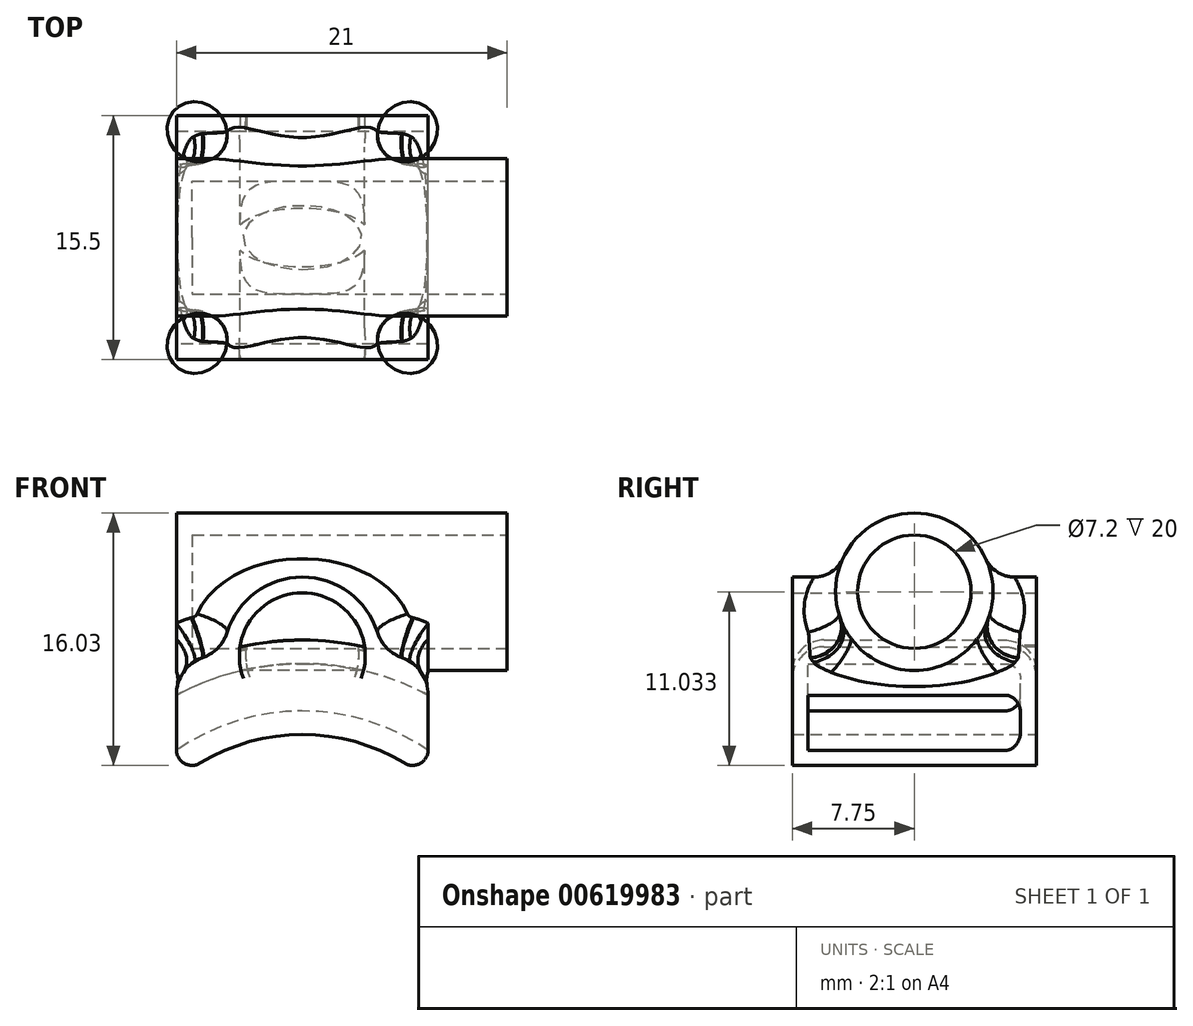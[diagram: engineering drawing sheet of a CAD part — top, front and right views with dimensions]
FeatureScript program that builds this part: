
annotation { "Feature Type Name" : "Feature", "Feature Type Description" : "" }
export const myFeature = defineFeature(function(context is Context, id is Id, definition is map)
    precondition{}
    {
        {
            var Q0;
            Q0=qCreatedBy(makeId("Front.planeOp"),FACE);
            var sketch = newSketch(context, id + "F0", { "sketchPlane" : qUnion([Q0])});
            skArc(sketch, "E0", {"start": v(8, 9.6) * mm, "mid": v(0, 12.5) * mm, "end": v(-8, 9.6) * mm});
            skArc(sketch, "E1.0", {"start": v(8, 11.49) * mm, "mid": v(0, 14) * mm, "end": v(-8, 11.49) * mm});
            skLineSegment(sketch, "E2", {"start": v(-8, 11.49) * mm, "end": v(-8, 9.6) * mm});
            skLineSegment(sketch, "E3", {"start": v(8, 11.49) * mm, "end": v(8, 9.6) * mm});
            skArc(sketch, "E4.0", {"start": v(8, 15) * mm, "mid": v(0, 17) * mm, "end": v(-8, 15) * mm});
            skLineSegment(sketch, "E5", {"start": v(-8, 15) * mm, "end": v(-8, 16.68) * mm});
            skLineSegment(sketch, "E6", {"start": v(8, 15) * mm, "end": v(8, 16.68) * mm});
            skArc(sketch, "E7.0", {"start": v(8, 16.68) * mm, "mid": v(0, 18.5) * mm, "end": v(-8, 16.68) * mm});
            skPoint(sketch, "E8.end.orphan", {"position": v(-8, 29.56) * mm});
            skPoint(sketch, "E8.start.orphan", {"position": v(8, 29.56) * mm});
            skArc(sketch, "E9", {"start": v(5, 17.81) * mm, "mid": v(0, 22.5) * mm, "end": v(-5, 17.81) * mm});
            skPoint(sketch, "E9.centerSnap0", {"position": v(0, 17) * mm});
            skArc(sketch, "E10.0", {"start": v(3.96, 18.07) * mm, "mid": v(0, 21.5) * mm, "end": v(-3.96, 18.07) * mm});
            skSolve(sketch);
        }
        {
            var Q0;
            Q0=qSketchRegion(id+"F0",true);
            extrude(context, id + "F1", {"entities" : qUnion([Q0]), "depth" : 13.5 * mm, "offsetDistance" : 25 * mm});
        }
        {
            var Q0;
            Q0=makeQuery(id+"F1.opExtrude","CAP_FACE",FACE,{"disambiguationData":[OSD([sQuery(id+"F0.wireOp",EDGE,"E0"),sQuery(id+"F0.wireOp",EDGE,"E1.0"),sQuery(id+"F0.wireOp",EDGE,"E2"),sQuery(id+"F0.wireOp",EDGE,"E3")])],"isStart":true});
            var sketch = newSketch(context, id + "F2", { "sketchPlane" : qUnion([Q0])});
            skCircle(sketch, "E11", {"center": v(0, 17.5) * mm, "radius": 3.6 * mm});
            skPoint(sketch, "E11.centerSnap0", {"position": v(0, 14) * mm});
            skCircle(sketch, "E12", {"center": v(0, 17.5) * mm, "radius": 5 * mm});
            skSolve(sketch);
        }
        {
            var Q0;
            Q0=qSketchRegion(id+"F2",true);
            extrude(context, id + "F3", {"entities" : qUnion([Q0]), "depth" : 1 * mm, "offsetDistance" : 25 * mm});
        }
        {
            var Q0;
            Q0=makeQuery(id+"F1.opExtrude","CAP_FACE",FACE,{"disambiguationData":[OSD([sQuery(id+"F0.wireOp",EDGE,"E4.0"),sQuery(id+"F0.wireOp",EDGE,"E5"),sQuery(id+"F0.wireOp",EDGE,"E6"),sQuery(id+"F0.wireOp",EDGE,"E7.0"),sQuery(id+"F0.wireOp",EDGE,"E9"),sQuery(id+"F0.wireOp",EDGE,"E10.0")])],"isStart":true});
            var sketch = newSketch(context, id + "F4", { "sketchPlane" : qUnion([Q0])});
            skArc(sketch, "E13.0", {"start": v(-3.54, 18.16) * mm, "mid": v(0, 13.9) * mm, "end": v(3.54, 18.16) * mm});
            skArc(sketch, "E14.0", {"start": v(-3.54, 18.16) * mm, "mid": v(0, 18.5) * mm, "end": v(3.54, 18.16) * mm});
            skSolve(sketch);
        }
        {
            var Q0;
            Q0=qSketchRegion(id+"F4",true);
            extrude(context, id + "F5", {"entities" : qUnion([Q0]), "depth" : 1 * mm, "offsetDistance" : 25 * mm});
        }
        {
            var Q0;
            Q0=makeQuery(id+"F1.opExtrude","CAP_FACE",FACE,{"disambiguationData":[OSD([sQuery(id+"F0.wireOp",EDGE,"E0"),sQuery(id+"F0.wireOp",EDGE,"E1.0"),sQuery(id+"F0.wireOp",EDGE,"E2"),sQuery(id+"F0.wireOp",EDGE,"E3")])],"isStart":true});
            var sketch = newSketch(context, id + "F6", { "sketchPlane" : qUnion([Q0])});
            skLineSegment(sketch, "E15.0", {"start": v(-8, 11.49) * mm, "end": v(-8, 9.6) * mm});
            skLineSegment(sketch, "E15.2", {"start": v(8, 9.6) * mm, "end": v(8, 11.49) * mm});
            skArc(sketch, "E15.3", {"start": v(-8, 9.6) * mm, "mid": v(0, 12.5) * mm, "end": v(8, 9.6) * mm});
            skArc(sketch, "E16.0", {"start": v(-8, 16.68) * mm, "mid": v(-6.52, 17.31) * mm, "end": v(-5, 17.81) * mm});
            skArc(sketch, "E17.0", {"start": v(5, 17.81) * mm, "mid": v(6.52, 17.31) * mm, "end": v(8, 16.68) * mm});
            skLineSegment(sketch, "E18.0", {"start": v(-8, 15) * mm, "end": v(-8, 16.68) * mm});
            skLineSegment(sketch, "E19.0", {"start": v(8, 15) * mm, "end": v(8, 16.68) * mm});
            skArc(sketch, "E20.0", {"start": v(-5, 17.81) * mm, "mid": v(0, 12.5) * mm, "end": v(5, 17.81) * mm});
            skLineSegment(sketch, "E21", {"start": v(-8, 15) * mm, "end": v(-8, 11.49) * mm});
            skLineSegment(sketch, "E22", {"start": v(8, 15) * mm, "end": v(8, 11.49) * mm});
            skSolve(sketch);
        }
        {
            var Q0;
            Q0=qSketchRegion(id+"F6",true);
            extrude(context, id + "F7", {"entities" : qUnion([Q0]), "depth" : 1 * mm, "offsetDistance" : 25 * mm});
        }
        {
            var Q0;
            Q0=makeQuery(id+"F1.opExtrude","CAP_FACE",FACE,{"disambiguationData":[OSD([sQuery(id+"F0.wireOp",EDGE,"E0"),sQuery(id+"F0.wireOp",EDGE,"E1.0"),sQuery(id+"F0.wireOp",EDGE,"E2"),sQuery(id+"F0.wireOp",EDGE,"E3")])],"isStart":false});
            var sketch = newSketch(context, id + "F8", { "sketchPlane" : qUnion([Q0])});
            skArc(sketch, "E23.0", {"start": v(8, 9.6) * mm, "mid": v(0, 12.5) * mm, "end": v(-8, 9.6) * mm});
            skArc(sketch, "E24.0", {"start": v(8, 16.68) * mm, "mid": v(0, 18.5) * mm, "end": v(-8, 16.68) * mm});
            skLineSegment(sketch, "E25", {"start": v(-8, 9.6) * mm, "end": v(-8, 16.68) * mm});
            skLineSegment(sketch, "E26", {"start": v(8, 9.6) * mm, "end": v(8, 16.68) * mm});
            skArc(sketch, "E27.0", {"start": v(5, 17.81) * mm, "mid": v(0, 22.5) * mm, "end": v(-5, 17.81) * mm});
            skArc(sketch, "E28.0", {"start": v(3.96, 18.07) * mm, "mid": v(0, 21.5) * mm, "end": v(-3.96, 18.07) * mm});
            skSolve(sketch);
        }
        {
            var Q0;
            Q0=qSketchRegion(id+"F8",true);
            extrude(context, id + "F9", {"entities" : qUnion([Q0]), "depth" : 1 * mm, "offsetDistance" : 25 * mm});
        }
        {
            var Q0;
            Q0=makeQuery(id+"F1.opExtrude","SWEPT_BODY",BODY,{"disambiguationData":[OSD([sQuery(id+"F0.wireOp",EDGE,"E4.0"),sQuery(id+"F0.wireOp",EDGE,"E5"),sQuery(id+"F0.wireOp",EDGE,"E6"),sQuery(id+"F0.wireOp",EDGE,"E7.0"),sQuery(id+"F0.wireOp",EDGE,"E9"),sQuery(id+"F0.wireOp",EDGE,"E10.0")])]});
            var Q1;
            Q1=makeQuery(id+"F3.opExtrude","SWEPT_BODY",BODY,{"disambiguationData":[OSD([sQuery(id+"F2.wireOp",EDGE,"E11"),sQuery(id+"F2.wireOp",EDGE,"E12")])]});
            var Q2;
            Q2=makeQuery(id+"F1.opExtrude","SWEPT_BODY",BODY,{"disambiguationData":[OSD([sQuery(id+"F0.wireOp",EDGE,"E0"),sQuery(id+"F0.wireOp",EDGE,"E1.0"),sQuery(id+"F0.wireOp",EDGE,"E2"),sQuery(id+"F0.wireOp",EDGE,"E3")])]});
            var Q3;
            Q3=makeQuery(id+"F7.opExtrude","SWEPT_BODY",BODY,{"disambiguationData":[OSD([sQuery(id+"F6.wireOp",EDGE,"E15.2"),sQuery(id+"F6.wireOp",EDGE,"E15.3"),sQuery(id+"F6.wireOp",EDGE,"E17.0"),sQuery(id+"F6.wireOp",EDGE,"E19.0"),sQuery(id+"F6.wireOp",EDGE,"E20.0"),sQuery(id+"F6.wireOp",EDGE,"E22")])]});
            var Q4;
            Q4=makeQuery(id+"F7.opExtrude","SWEPT_BODY",BODY,{"disambiguationData":[OSD([sQuery(id+"F6.wireOp",EDGE,"E15.0"),sQuery(id+"F6.wireOp",EDGE,"E15.3"),sQuery(id+"F6.wireOp",EDGE,"E16.0"),sQuery(id+"F6.wireOp",EDGE,"E18.0"),sQuery(id+"F6.wireOp",EDGE,"E20.0"),sQuery(id+"F6.wireOp",EDGE,"E21")])]});
            var Q5;
            Q5=makeQuery(id+"F5.opExtrude","SWEPT_BODY",BODY,{"disambiguationData":[OSD([sQuery(id+"F4.wireOp",EDGE,"E13.0"),sQuery(id+"F4.wireOp",EDGE,"E14.0")])]});
            var Q6;
            Q6=makeQuery(id+"F9.opExtrude","SWEPT_BODY",BODY,{"disambiguationData":[OSD([sQuery(id+"F8.wireOp",EDGE,"E23.0"),sQuery(id+"F8.wireOp",EDGE,"E24.0"),sQuery(id+"F8.wireOp",EDGE,"E25"),sQuery(id+"F8.wireOp",EDGE,"E26")])]});
            booleanBodies(context, id + "F10", {"operationType" : BooleanOperationType.UNION, "tools" : qUnion([Q0, Q1, Q2, Q3, Q4, Q5, Q6])});
        }
        {
            var Q0;
            Q0=makeQuery(id+"F5.opExtrude","CAP_EDGE",EDGE,{"disambiguationData":[OSD([sQuery(id+"F4.wireOp",EDGE,"E14.0")])],"isStart":false});
            var Q1;
            {var subQ0=sQuery(id+"F8.wireOp",EDGE,"E28.0");var subQ1=sQuery(id+"F8.wireOp",EDGE,"E24.0");Q1=makeQuery(id+"F9.opExtrude","CAP_EDGE",EDGE,{"disambiguationData":[OSD([subQ1]),TDD([makeQuery(id+"F8.imprint","IMPRINT",EDGE,{"disambiguationData":[TD([[makeQuery(id+"F8.imprint","INTERSECT",VERTEX,{"disambiguationData":[OD(0.0)],"derivedFrom":[subQ1,subQ0]}),-1.0]])],"derivedFrom":subQ1})])],"isStart":false});}
            fillet(context, id + "F11", {"entities" : qUnion([Q0, Q1]), "radius" : 2 * mm, "tangentPropagation" : true, "allowEdgeOverflow" : false});
        }
        {
            var Q0;
            {var subQ0=sQuery(id+"F0.wireOp",EDGE,"E9");var subQ1=sQuery(id+"F0.wireOp",EDGE,"E7.0");Q0=makeQuery(id+"F10.opBoolean","MERGE",EDGE,{"derivedFrom":[makeQuery(id+"F1.opExtrude","SWEPT_EDGE",EDGE,{"disambiguationData":[OSD([subQ1,subQ0]),TDD([makeQuery(id+"F0.imprint","INTERSECT",VERTEX,{"disambiguationData":[OD(1.0)],"derivedFrom":[subQ1,subQ0]})])]}),makeQuery(id+"F7.opExtrude","SWEPT_EDGE",EDGE,{"disambiguationData":[OSD([sQuery(id+"F6.wireOp",EDGE,"E17.0"),sQuery(id+"F6.wireOp",EDGE,"E20.0")])]})]});}
            var Q1;
            Q1=makeQuery(id+"F10.opBoolean","MERGE",EDGE,{"derivedFrom":[makeQuery(id+"F1.opExtrude","SWEPT_EDGE",EDGE,{"disambiguationData":[OSD([sQuery(id+"F0.wireOp",EDGE,"E5"),sQuery(id+"F0.wireOp",EDGE,"E7.0")])]}),makeQuery(id+"F7.opExtrude","SWEPT_EDGE",EDGE,{"disambiguationData":[OSD([sQuery(id+"F6.wireOp",EDGE,"E17.0"),sQuery(id+"F6.wireOp",EDGE,"E19.0")])]}),makeQuery(id+"F9.opExtrude","SWEPT_EDGE",EDGE,{"disambiguationData":[OSD([sQuery(id+"F8.wireOp",EDGE,"E24.0"),sQuery(id+"F8.wireOp",EDGE,"E25")])]})]});
            var Q2;
            {var subQ0=sQuery(id+"F0.wireOp",EDGE,"E9");var subQ1=sQuery(id+"F0.wireOp",EDGE,"E7.0");Q2=makeQuery(id+"F10.opBoolean","MERGE",EDGE,{"derivedFrom":[makeQuery(id+"F1.opExtrude","SWEPT_EDGE",EDGE,{"disambiguationData":[OSD([subQ1,subQ0]),TDD([makeQuery(id+"F0.imprint","INTERSECT",VERTEX,{"disambiguationData":[OD(0.0)],"derivedFrom":[subQ1,subQ0]})])]}),makeQuery(id+"F7.opExtrude","SWEPT_EDGE",EDGE,{"disambiguationData":[OSD([sQuery(id+"F6.wireOp",EDGE,"E16.0"),sQuery(id+"F6.wireOp",EDGE,"E20.0")])]})]});}
            var Q3;
            Q3=makeQuery(id+"F10.opBoolean","MERGE",EDGE,{"derivedFrom":[makeQuery(id+"F1.opExtrude","SWEPT_EDGE",EDGE,{"disambiguationData":[OSD([sQuery(id+"F0.wireOp",EDGE,"E6"),sQuery(id+"F0.wireOp",EDGE,"E7.0")])]}),makeQuery(id+"F7.opExtrude","SWEPT_EDGE",EDGE,{"disambiguationData":[OSD([sQuery(id+"F6.wireOp",EDGE,"E16.0"),sQuery(id+"F6.wireOp",EDGE,"E18.0")])]}),makeQuery(id+"F9.opExtrude","SWEPT_EDGE",EDGE,{"disambiguationData":[OSD([sQuery(id+"F8.wireOp",EDGE,"E24.0"),sQuery(id+"F8.wireOp",EDGE,"E26")])]})]});
            fillet(context, id + "F12", {"entities" : qUnion([Q0, Q1, Q2, Q3]), "radius" : 2.5 * mm, "tangentPropagation" : true, "allowEdgeOverflow" : false});
        }
        {
            var Q0;
            Q0=makeQuery(id+"F10.opBoolean","MERGE",EDGE,{"derivedFrom":[makeQuery(id+"F1.opExtrude","SWEPT_EDGE",EDGE,{"disambiguationData":[OSD([sQuery(id+"F0.wireOp",EDGE,"E0"),sQuery(id+"F0.wireOp",EDGE,"E2")])]}),makeQuery(id+"F7.opExtrude","SWEPT_EDGE",EDGE,{"disambiguationData":[OSD([sQuery(id+"F6.wireOp",EDGE,"E15.2"),sQuery(id+"F6.wireOp",EDGE,"E15.3")])]}),makeQuery(id+"F9.opExtrude","SWEPT_EDGE",EDGE,{"disambiguationData":[OSD([sQuery(id+"F8.wireOp",EDGE,"E23.0"),sQuery(id+"F8.wireOp",EDGE,"E25")])]})]});
            var Q1;
            Q1=makeQuery(id+"F10.opBoolean","MERGE",EDGE,{"derivedFrom":[makeQuery(id+"F1.opExtrude","SWEPT_EDGE",EDGE,{"disambiguationData":[OSD([sQuery(id+"F0.wireOp",EDGE,"E0"),sQuery(id+"F0.wireOp",EDGE,"E3")])]}),makeQuery(id+"F7.opExtrude","SWEPT_EDGE",EDGE,{"disambiguationData":[OSD([sQuery(id+"F6.wireOp",EDGE,"E15.0"),sQuery(id+"F6.wireOp",EDGE,"E15.3")])]}),makeQuery(id+"F9.opExtrude","SWEPT_EDGE",EDGE,{"disambiguationData":[OSD([sQuery(id+"F8.wireOp",EDGE,"E23.0"),sQuery(id+"F8.wireOp",EDGE,"E26")])]})]});
            fillet(context, id + "F13", {"entities" : qUnion([Q0, Q1]), "radius" : 1 * mm, "tangentPropagation" : true, "allowEdgeOverflow" : false});
        }
        {
            var Q0;
            {var subQ0=sQuery(id+"F6.wireOp",EDGE,"E20.0");var subQ1=sQuery(id+"F6.wireOp",EDGE,"E15.3");Q0=makeQuery(id+"F10.opBoolean","INTERSECT",EDGE,{"derivedFrom":[makeQuery(id+"F3.opExtrude","CAP_FACE",FACE,{"disambiguationData":[OSD([sQuery(id+"F2.wireOp",EDGE,"E11"),sQuery(id+"F2.wireOp",EDGE,"E12")])],"isStart":true}),makeQuery(id+"F5.opExtrude","CAP_FACE",FACE,{"disambiguationData":[OSD([sQuery(id+"F4.wireOp",EDGE,"E13.0"),sQuery(id+"F4.wireOp",EDGE,"E14.0")])],"isStart":true}),makeQuery(id+"F7.opExtrude","CAP_FACE",FACE,{"disambiguationData":[OSD([sQuery(id+"F6.wireOp",EDGE,"E15.0"),subQ1,sQuery(id+"F6.wireOp",EDGE,"E16.0"),sQuery(id+"F6.wireOp",EDGE,"E18.0"),subQ0,sQuery(id+"F6.wireOp",EDGE,"E21")])],"isStart":true}),makeQuery(id+"F7.opExtrude","CAP_FACE",FACE,{"disambiguationData":[OSD([sQuery(id+"F6.wireOp",EDGE,"E15.2"),subQ1,sQuery(id+"F6.wireOp",EDGE,"E17.0"),sQuery(id+"F6.wireOp",EDGE,"E19.0"),subQ0,sQuery(id+"F6.wireOp",EDGE,"E22")])],"isStart":true})]});}
            var Q1;
            Q1=makeQuery(id+"F1.opExtrude","CAP_EDGE",EDGE,{"disambiguationData":[OSD([sQuery(id+"F0.wireOp",EDGE,"E4.0")])],"isStart":true});
            var Q2;
            Q2=makeQuery(id+"F1.opExtrude","CAP_EDGE",EDGE,{"disambiguationData":[OSD([sQuery(id+"F0.wireOp",EDGE,"E1.0")])],"isStart":false});
            var Q3;
            Q3=makeQuery(id+"F1.opExtrude","CAP_EDGE",EDGE,{"disambiguationData":[OSD([sQuery(id+"F0.wireOp",EDGE,"E4.0")])],"isStart":false});
            fillet(context, id + "F14", {"entities" : qUnion([Q0, Q1, Q2, Q3]), "radius" : 1 * mm, "tangentPropagation" : true, "allowEdgeOverflow" : false});
        }
        {
            var Q0;
            Q0=qCreatedBy(makeId("Right.planeOp"),FACE);
            var sketch = newSketch(context, id + "F15", { "sketchPlane" : qUnion([Q0])});
            skCircle(sketch, "E29", {"center": v(-6.75, 21.57) * mm, "radius": 5 * mm});
            skSolve(sketch);
        }
        {
            var Q0;
            Q0 = qSketchRegion(id + "F15", true);
            extrude(context, id + "F16", {"entities" : qUnion([Q0]), "operationType" : NewBodyOperationType.ADD, "endBound" : BoundingType.SYMMETRIC, "depth" : 16 * mm, "offsetDistance" : 25 * mm});
        }
        {
            var Q0;
            Q0=makeQuery(id+"F16.opExtrude","CAP_FACE",FACE,{"disambiguationData":[OSD([sQuery(id+"F15.wireOp",EDGE,"E29")])],"isStart":false});
            var sketch = newSketch(context, id + "F17", { "sketchPlane" : qUnion([Q0])});
            skCircle(sketch, "E30", {"center": v(-6.75, 21.57) * mm, "radius": 3.6 * mm});
            skSolve(sketch);
        }
        {
            var Q0;
            Q0 = qSketchRegion(id + "F17", true);
            extrude(context, id + "F18", {"entities" : qUnion([Q0]), "operationType" : NewBodyOperationType.REMOVE, "endBound" : BoundingType.THROUGH_ALL, "oppositeDirection" : true, "depth" : 25 * mm, "offsetDistance" : 25 * mm});
        }
        {
            var Q0;
            Q0=makeQuery(id+"F9.opExtrude","CAP_FACE",FACE,{"disambiguationData":[OSD([sQuery(id+"F8.wireOp",EDGE,"E23.0"),sQuery(id+"F8.wireOp",EDGE,"E24.0"),sQuery(id+"F8.wireOp",EDGE,"E25"),sQuery(id+"F8.wireOp",EDGE,"E26"),sQuery(id+"F8.wireOp",EDGE,"E27.0"),sQuery(id+"F8.wireOp",EDGE,"E28.0")])],"isStart":false});
            var sketch = newSketch(context, id + "F19", { "sketchPlane" : qUnion([Q0])});
            skLineSegment(sketch, "E31", {"start": v(0, 27.62) * mm, "end": v(0, 5.28) * mm});
            skArc(sketch, "E32.0", {"start": v(-3.96, 18.07) * mm, "mid": v(0, 18.5) * mm, "end": v(3.96, 18.07) * mm});
            skArc(sketch, "E33.0", {"start": v(3.96, 18.07) * mm, "mid": v(0, 21.5) * mm, "end": v(-3.96, 18.07) * mm});
            skSolve(sketch);
        }
        {
            var Q0;
            Q0 = qSketchRegion(id + "F19", true);
            extrude(context, id + "F20", {"entities" : qUnion([Q0]), "operationType" : NewBodyOperationType.REMOVE, "endBound" : BoundingType.THROUGH_ALL, "oppositeDirection" : true, "depth" : 25 * mm, "offsetDistance" : 25 * mm});
        }
        {
            var Q0;
            Q0=makeQuery(id+"F16.boolean.opBoolean","INTERSECT",EDGE,{"disambiguationData":[OD(1.0)],"derivedFrom":[makeQuery(id+"F10.opBoolean","MERGE",FACE,{"derivedFrom":[makeQuery(id+"F1.opExtrude","SWEPT_FACE",FACE,{"disambiguationData":[OSD([sQuery(id+"F0.wireOp",EDGE,"E9")])]}),makeQuery(id+"F3.opExtrude","SWEPT_FACE",FACE,{"disambiguationData":[OSD([sQuery(id+"F2.wireOp",EDGE,"E12")])]}),makeQuery(id+"F9.opExtrude","SWEPT_FACE",FACE,{"disambiguationData":[OSD([sQuery(id+"F8.wireOp",EDGE,"E27.0")])]})]}),makeQuery(id+"F16.opExtrude","SWEPT_FACE",FACE,{"disambiguationData":[OSD([sQuery(id+"F15.wireOp",EDGE,"E29")])]})]});
            fillet(context, id + "F21", {"entities" : qUnion([Q0]), "radius" : 2 * mm, "tangentPropagation" : true, "allowEdgeOverflow" : false});
        }
        {
            var Q0;
            Q0=makeQuery(id+"F16.opExtrude","CAP_FACE",FACE,{"disambiguationData":[OSD([sQuery(id+"F15.wireOp",EDGE,"E29")])],"isStart":false});
            var sketch = newSketch(context, id + "F22", { "sketchPlane" : qUnion([Q0])});
            skCircle(sketch, "E34.0", {"center": v(-6.75, 21.57) * mm, "radius": 3.6 * mm});
            skCircle(sketch, "E35", {"center": v(-6.75, 21.57) * mm, "radius": 5 * mm});
            skSolve(sketch);
        }
        {
            var Q0;
            Q0 = qSketchRegion(id + "F22", true);
            extrude(context, id + "F23", {"entities" : qUnion([Q0]), "operationType" : NewBodyOperationType.ADD, "depth" : 5 * mm, "offsetDistance" : 25 * mm});
        }
        {
            var Q0;
            Q0=makeQuery(id+"F16.opExtrude","CAP_FACE",FACE,{"disambiguationData":[OSD([sQuery(id+"F15.wireOp",EDGE,"E29")])],"isStart":true});
            var sketch = newSketch(context, id + "F24", { "sketchPlane" : qUnion([Q0])});
            skCircle(sketch, "E36.0", {"center": v(6.75, 21.57) * mm, "radius": 3.6 * mm});
            skSolve(sketch);
        }
        {
            var Q0;
            Q0 = qSketchRegion(id + "F24", true);
            extrude(context, id + "F25", {"entities" : qUnion([Q0]), "operationType" : NewBodyOperationType.ADD, "oppositeDirection" : true, "depth" : 1 * mm, "offsetDistance" : 25 * mm});
        }
    });
